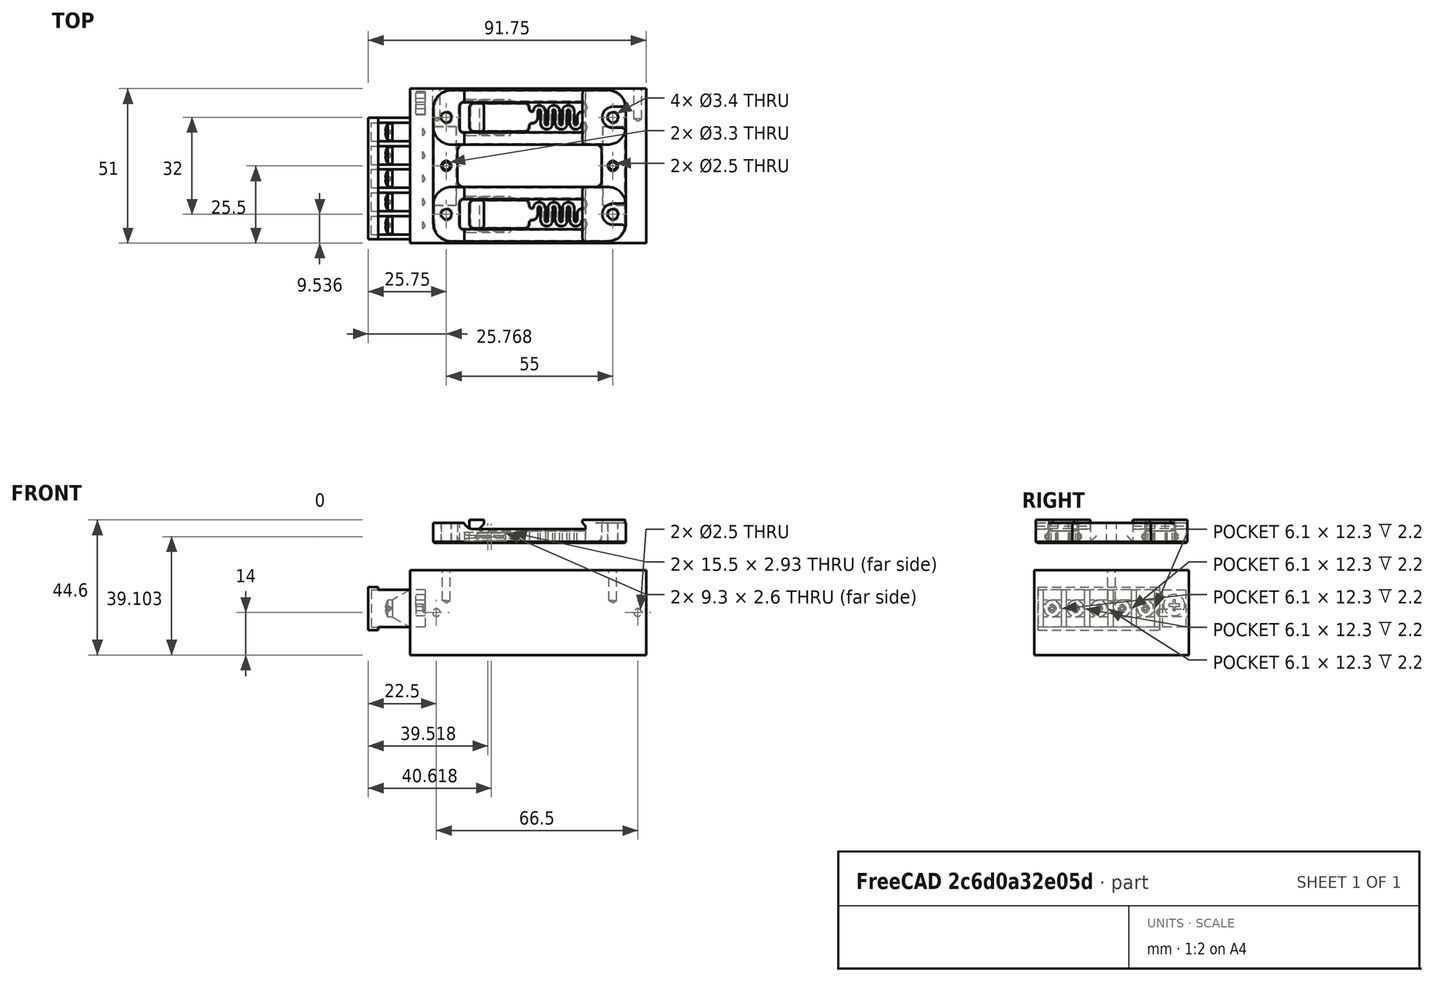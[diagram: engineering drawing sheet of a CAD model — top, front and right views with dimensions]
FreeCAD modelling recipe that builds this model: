
FCSTD DOCUMENT  (FreeCAD 0.18R16146 (Git))
Label: PSU-RS-25
License: Other
LicenseURL: GPL3
objects: Part::Feature×4, Part::MultiFuse×3, Part::Box×2, Part::Cylinder×2, Part::Chamfer×1, Part::Cut×1, Part::Fillet×1
note: 14 computed .brp shape members not serialized (recipe doc carries the construction recipe); baked Part::Feature solids carry a one-line shape summary decoded from their .brp

FEATURE [Part::Feature] Part__Feature822  label="RS-25 PSU Bracket"
  Placement = pos=(-0.481859,8.39696,12.1031) rot=(0,1,0;3.14159rad)
  shape: bbox 63.6 x 18 x 7.6 mm, 163 faces (baked)
FEATURE [Part::Box] Box  label="Cube"
  AttacherType = Attacher::AttachEngine3D
  Height = 6.6
  Length = 8
  Placement = pos=(-32.28,8,0) rot=(0,0,1;0rad)
  Width = 26
FEATURE [Part::Feature] Fusion006002011004053036004001028003005006  label="RS-25-5-PSU"
  Placement = pos=(-1,21,-9) rot=(-1,0,0;1.5708rad)
  shape: bbox 91.75 x 51 x 28 mm, 292 faces (baked)
FEATURE [Part::Feature] Part__Feature823  label="RS-25 PSU Bracket001"
  Placement = pos=(-0.481859,40.397,12.1031) rot=(0,1,0;3.14159rad)
  shape: bbox 63.6 x 18 x 7.6 mm, 163 faces (baked)
FEATURE [Part::Cylinder] Cylinder
  Angle = 360
  AttacherType = Attacher::AttachEngine3D
  Height = 10
  Placement = pos=(-28,21,0) rot=(0,0,1;0rad)
  Radius = 1.65
FEATURE [Part::Cylinder] Cylinder001
  Angle = 360
  AttacherType = Attacher::AttachEngine3D
  Height = 10
  Placement = pos=(27,21,0) rot=(0,0,1;0rad)
  Radius = 1.65
FEATURE [Part::Box] Box001  label="Cube001"
  AttacherType = Attacher::AttachEngine3D
  Height = 6.6
  Length = 8
  Placement = pos=(23.32,8,0) rot=(0,0,1;0rad)
  Width = 26
FEATURE [Part::MultiFuse] Fusion006002011004053036004001028003005007
  Shapes = -> [Cylinder,Cylinder001]
FEATURE [Part::MultiFuse] Fusion
  Shapes = -> [Box,Box001]
FEATURE [Part::Chamfer] Chamfer
  Base = -> Fusion
  Edges = 4 edges r=0.4: [Edge4,Edge8,Edge16,Edge20]
FEATURE [Part::Cut] Cut
  Base = -> Chamfer
  Tool = -> Fusion006002011004053036004001028003005007
FEATURE [Part::MultiFuse] Fusion006002011004053036004001028003005008
  Shapes = -> [Cut,Part__Feature823,Part__Feature822]
FEATURE [Part::Fillet] Fillet
  Base = -> Fusion006002011004053036004001028003005008
  Edges = 4 edges r=2: [Edge236,Edge245,Edge288,Edge351]
FEATURE [Part::Feature] Fillet001
  shape: bbox 63.6 x 50 x 7.603 mm, 347 faces (baked)
